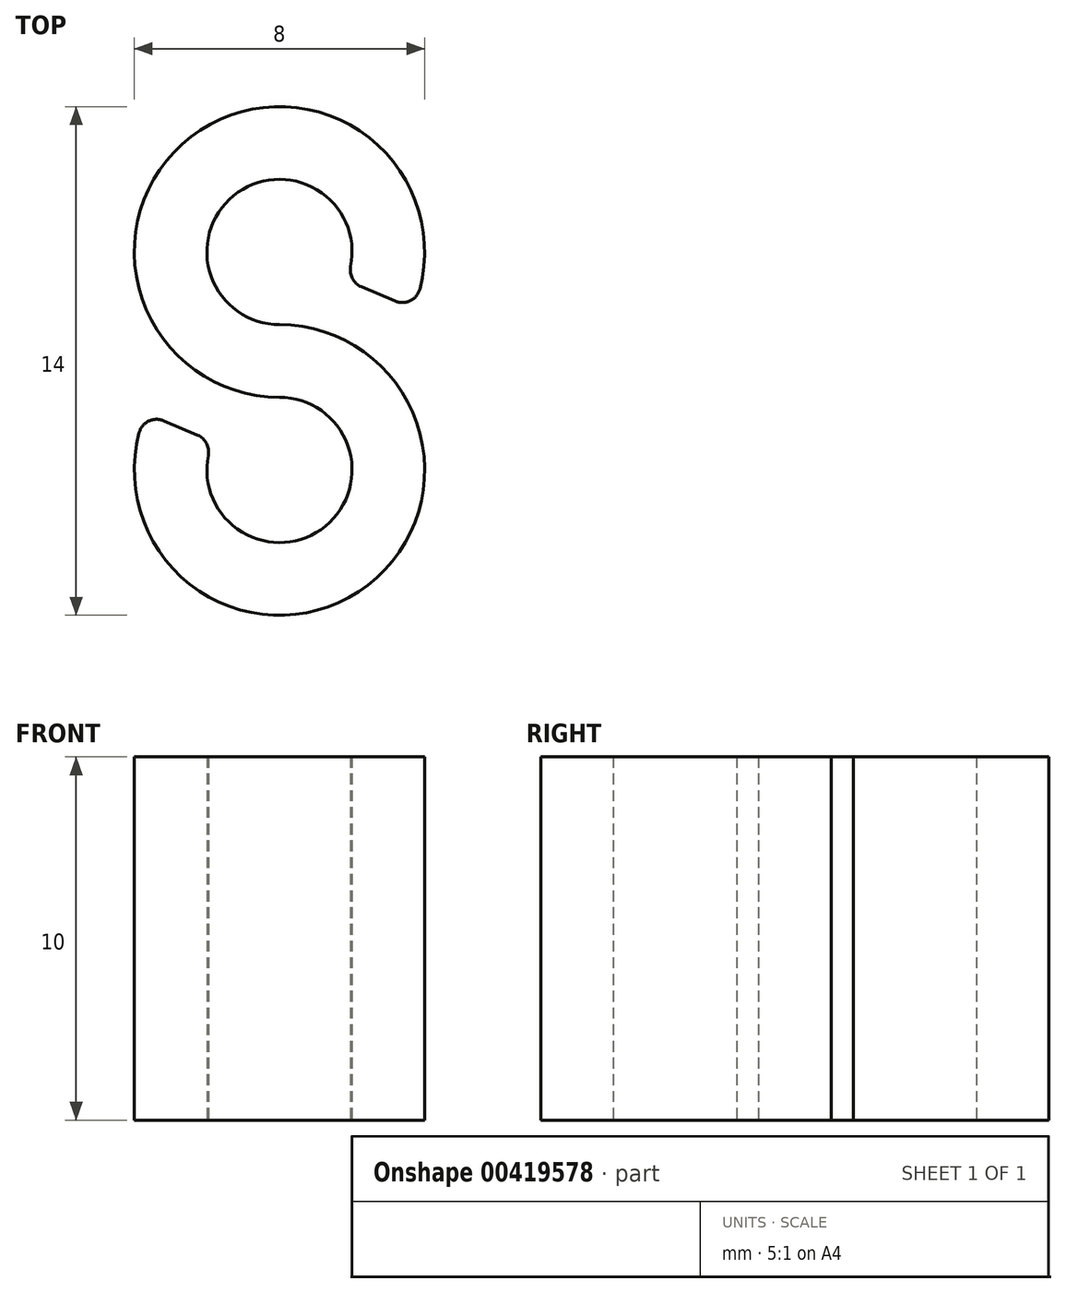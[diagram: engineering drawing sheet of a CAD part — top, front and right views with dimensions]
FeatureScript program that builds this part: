
annotation { "Feature Type Name" : "Feature", "Feature Type Description" : "" }
export const myFeature = defineFeature(function(context is Context, id is Id, definition is map)
    precondition{}
    {
        {
            var Q0;
            Q0=qCreatedBy(makeId("Top.planeOp"),FACE);
            var sketch = newSketch(context, id + "F0", { "sketchPlane" : qUnion([Q0])});
            skArc(sketch, "E0", {"start": v(1.96, -0.4) * mm, "mid": v(-1.27, 1.55) * mm, "end": v(0, -2) * mm});
            skArc(sketch, "E1", {"start": v(3.87, -1.02) * mm, "mid": v(-2.44, 3.17) * mm, "end": v(0, -4) * mm});
            skArc(sketch, "E2", {"start": v(-1.96, -5.6) * mm, "mid": v(1.27, -7.55) * mm, "end": v(0, -4) * mm});
            skArc(sketch, "E3", {"start": v(-3.87, -4.98) * mm, "mid": v(2.44, -9.17) * mm, "end": v(0, -2) * mm});
            skLineSegment(sketch, "E4", {"start": v(0, -6) * mm, "end": v(-5.65, -6) * mm, "construction": true});
            skLineSegment(sketch, "E5", {"start": v(0, 0) * mm, "end": v(7.17, 0) * mm, "construction": true});
            skLineSegment(sketch, "E6", {"start": v(2.25, -0.96) * mm, "end": v(3.19, -1.35) * mm});
            skLineSegment(sketch, "E7", {"start": v(-2.25, -5.04) * mm, "end": v(-3.19, -4.65) * mm});
            skPoint(sketch, "E8.visualSharp", {"position": v(-1.84, -5.22) * mm});
            skArc(sketch, "E8.filletArc", {"start": v(-1.96, -5.6) * mm, "mid": v(-2, -5.27) * mm, "end": v(-2.25, -5.04) * mm});
            skPoint(sketch, "E9.visualSharp", {"position": v(-3.68, -4.44) * mm});
            skArc(sketch, "E9.filletArc", {"start": v(-3.19, -4.65) * mm, "mid": v(-3.6, -4.66) * mm, "end": v(-3.87, -4.98) * mm});
            skPoint(sketch, "E10.visualSharp", {"position": v(1.84, -0.78) * mm});
            skArc(sketch, "E10.filletArc", {"start": v(1.96, -0.4) * mm, "mid": v(2, -0.73) * mm, "end": v(2.25, -0.96) * mm});
            skPoint(sketch, "E11.visualSharp", {"position": v(3.68, -1.56) * mm});
            skArc(sketch, "E11.filletArc", {"start": v(3.19, -1.35) * mm, "mid": v(3.6, -1.34) * mm, "end": v(3.87, -1.02) * mm});
            skSolve(sketch);
        }
        {
            var Q0;
            Q0 = qSketchRegion(id + "F0", true);
            extrude(context, id + "F1", {"entities" : qUnion([Q0]), "depth" : 10 * mm});
        }
    });
